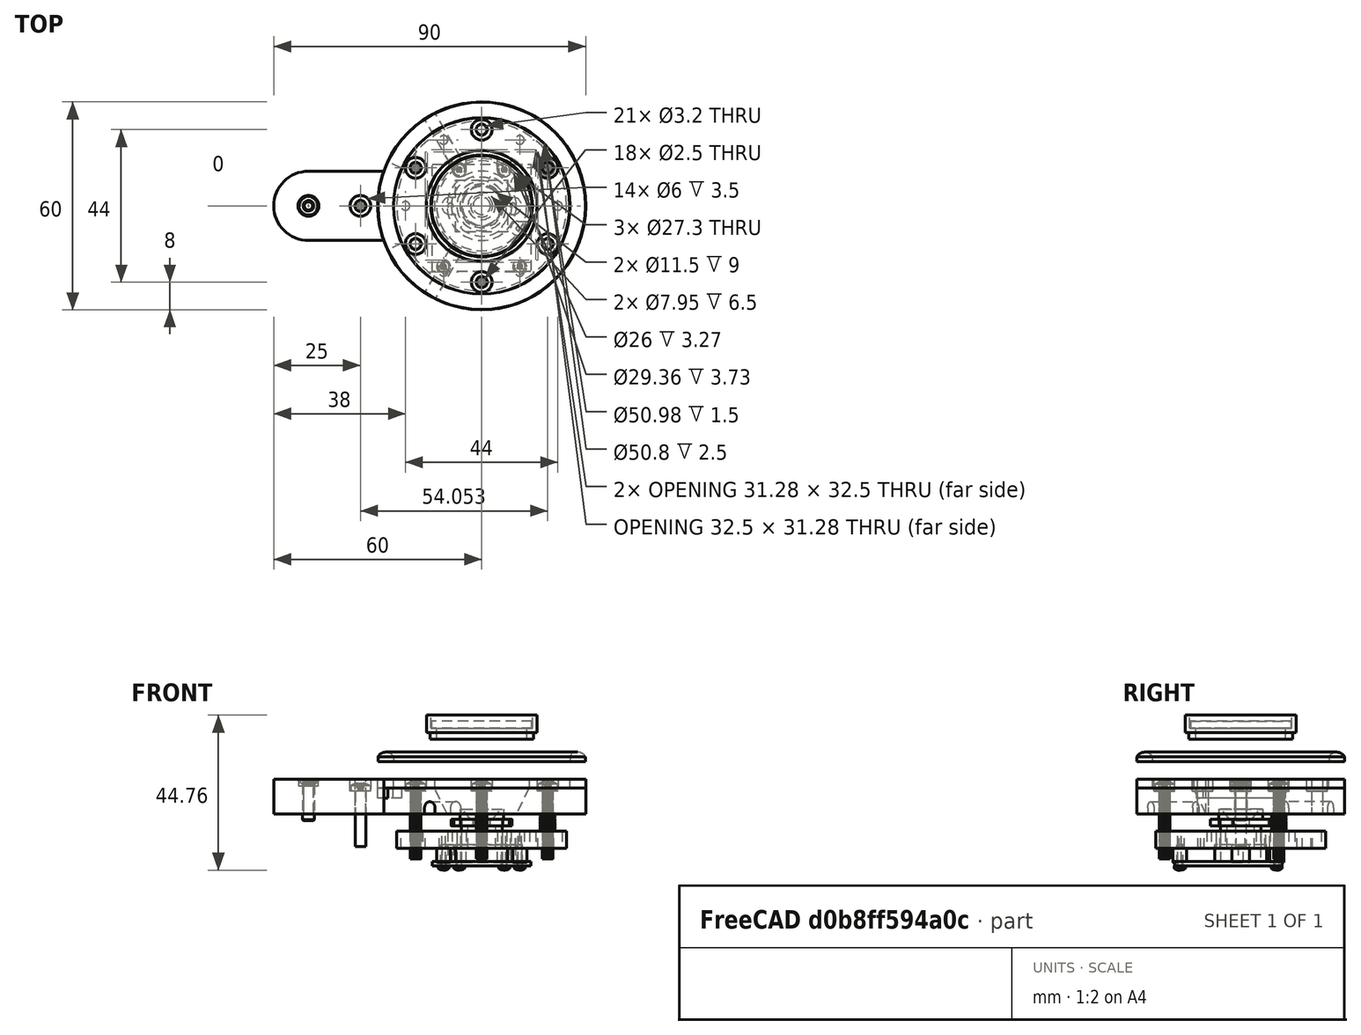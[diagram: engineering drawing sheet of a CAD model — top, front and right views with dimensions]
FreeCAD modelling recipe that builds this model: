
FCSTD DOCUMENT  (FreeCAD 0.15R4671 (Git))
Label: UpCam_base_v1
License: CreativeCommons Attribution-ShareAlike
LicenseURL: http://creativecommons.org/licenses/by-sa/4.0/
objects: Sketcher::SketchObject×10, Part::FeaturePython×10, Part::Feature×6, PartDesign::Pocket×5, PartDesign::Pad×4, Part::Mirroring×4, Part::Cut×2, PartDesign::Revolution×1, Part::MultiFuse×1
note: 53 computed .brp shape members not serialized (recipe doc carries the construction recipe); baked Part::Feature solids carry a one-line shape summary decoded from their .brp

FEATURE [Part::Feature] Compound  label="Philips SPZ5000 webcam"
  Placement = pos=(0,0,-15) rot=(0,0,1;1.5708rad)
  shape: bbox 28.5 x 31 x 16.4 mm, 52 faces, 3 solids (baked)
FEATURE [Sketcher::SketchObject] Sketch  label="camera base"
  sketch-geometry (20):
    g0: LineSegment [constr] StartX=-50 StartY=0 StartZ=0 EndX=0 EndY=0 EndZ=0
    g1: Circle CenterX=-50 CenterY=0 CenterZ=0 NormalX=0 NormalY=0 NormalZ=1 Radius=1.5
    g2: LineSegment StartX=-28.2843 StartY=10 StartZ=0 EndX=-50 EndY=10 EndZ=0
    g3: LineSegment StartX=-50 StartY=-10 StartZ=0 EndX=-28.2843 EndY=-10 EndZ=0
    g4: ArcOfCircle CenterX=-50 CenterY=0 CenterZ=0 NormalX=0 NormalY=0 NormalZ=1 Radius=10 StartAngle=1.5708 EndAngle=4.71239
    g5: ArcOfCircle CenterX=0 CenterY=0 CenterZ=0 NormalX=0 NormalY=0 NormalZ=1 Radius=30 StartAngle=3.48143 EndAngle=9.08494
    g6: Circle CenterX=-35 CenterY=0 CenterZ=0 NormalX=0 NormalY=0 NormalZ=1 Radius=1.6
    g7: LineSegment [constr] StartX=19.0526 StartY=-11 StartZ=0 EndX=19.0526 EndY=11 EndZ=0
    g8: LineSegment [constr] StartX=19.0526 StartY=11 StartZ=0 EndX=0 EndY=22 EndZ=0
    g9: LineSegment [constr] StartX=0 StartY=22 StartZ=0 EndX=-19.0526 EndY=11 EndZ=0
    g10: LineSegment [constr] StartX=-19.0526 StartY=11 StartZ=0 EndX=-19.0526 EndY=-11 EndZ=0
    g11: LineSegment [constr] StartX=-19.0526 StartY=-11 StartZ=0 EndX=0 EndY=-22 EndZ=0
    g12: LineSegment [constr] StartX=0 StartY=-22 StartZ=0 EndX=19.0526 EndY=-11 EndZ=0
    g13: Circle [constr] CenterX=0 CenterY=0 CenterZ=0 NormalX=0 NormalY=0 NormalZ=1 Radius=22
    g14: Circle CenterX=0 CenterY=22 CenterZ=0 NormalX=0 NormalY=0 NormalZ=1 Radius=1.6
    g15: Circle CenterX=-19.0526 CenterY=-11 CenterZ=0 NormalX=0 NormalY=0 NormalZ=1 Radius=1.6
    g16: Circle CenterX=19.0526 CenterY=-11 CenterZ=0 NormalX=0 NormalY=0 NormalZ=1 Radius=1.6
    g17: Circle CenterX=-19.0526 CenterY=11 CenterZ=0 NormalX=0 NormalY=0 NormalZ=1 Radius=1.6
    g18: Circle CenterX=0 CenterY=-22 CenterZ=0 NormalX=0 NormalY=0 NormalZ=1 Radius=1.6
    g19: Circle CenterX=19.0526 CenterY=11 CenterZ=0 NormalX=0 NormalY=0 NormalZ=1 Radius=1.6
  constraints (51):
    c: Horizontal(g0)
    c: DistanceX(g0) = 50
    c: Radius(g1) = 1.5
    c: Horizontal(g2)
    c: Horizontal(g3)
    c: Coincident(g4,g2)
    c: Coincident(g4,g3)
    c: Tangent(g4,g2)
    c: Radius(g4) = 10
    c: Coincident(g5,g0)
    c: Coincident(g5,g3)
    c: Coincident(g2,g5)
    c: Equal(g2,g3)
    c: DistanceX(g2,g3) = 0
    c: Coincident(g4,g1)
    c: Coincident(g0,g1)
    c: DistanceX(g0) = 0
    c: DistanceY(g0) = 0
    c: Radius(g5) = 30
    c: PointOnObject(g6,g0)
    c: DistanceX(g6,g0) = -15
    c: Coincident(g8,g9)
    c: Coincident(g9,g10)
    c: Coincident(g10,g11)
    c: Coincident(g11,g12)
    c: Coincident(g12,g7)
    c: Equal(g7, g8-g12) x5
    c: PointOnObject(g7,g13)
    c: PointOnObject(g8,g13)
    c: PointOnObject(g9,g13)
    c: PointOnObject(g10,g13)
    c: PointOnObject(g11,g13)
    c: PointOnObject(g12,g13)
    c: Coincident(g10,g-1)
    c: Coincident(g13,g-1)
    c: Radius(g13) = 22
    c: Coincident(g14,g8)
    c: Coincident(g15,g10)
    c: Coincident(g16,g7)
    c: Coincident(g17,g9)
    c: Coincident(g18,g11)
    c: Equal(g19,g16)
    c: Equal(g16,g18)
    c: Equal(g18,g15)
    c: Equal(g15,g17)
    c: Equal(g17,g14)
    c: Radius(g19) = 1.6
    c: Coincident(g19,g7)
    c: Coincident(g8,g7)
    c: Equal(g6,g14)
    c: Vertical(g10)
FEATURE [Sketcher::SketchObject] Sketch001
  Placement = pos=(0,0,0) rot=(1,0,0;1.5708rad)
  sketch-geometry (5):
    g0: LineSegment StartX=13.65 StartY=10 StartZ=0 EndX=13.65 EndY=7.5 EndZ=0
    g1: LineSegment StartX=13.65 StartY=7.5 StartZ=0 EndX=10 EndY=0 EndZ=0
    g2: LineSegment StartX=10 StartY=0 StartZ=0 EndX=0 EndY=0 EndZ=0
    g3: LineSegment StartX=0 StartY=0 StartZ=0 EndX=0 EndY=10 EndZ=0
    g4: LineSegment StartX=0 StartY=10 StartZ=0 EndX=13.65 EndY=10 EndZ=0
  constraints (14):
    c: Vertical(g0)
    c: Coincident(g0,g1)
    c: Coincident(g1,g2)
    c: Horizontal(g2)
    c: Coincident(g2,g3)
    c: Vertical(g3)
    c: Coincident(g3,g4)
    c: Coincident(g4,g0)
    c: Horizontal(g4)
    c: DistanceX(g2) = -10
    c: DistanceX(g4) = 13.65
    c: DistanceY(g0) = -2.5
    c: DistanceY(g3) = 10
    c: Coincident(g2,g-1)
FEATURE [PartDesign::Revolution] Revolution
  Angle = 360
  Axis = (0,0,1)
  Base = (0,0,0)
  Placement = pos=(0,0,0) rot=(1,0,0;1.5708rad)
  ReferenceAxis = -> Sketch001 [V_Axis]
  Reversed = true
  Sketch = -> Sketch001
FEATURE [PartDesign::Pad] Pad
  Length = 10
  Length2 = 100
  Sketch = -> Sketch
  Type = 0
FEATURE [Part::Cut] Cut
  Base = -> Pad
  Tool = -> Revolution
FEATURE [Sketcher::SketchObject] Sketch002
  ExternalGeometry = -> [Cut]
  Placement = pos=(0,0,10) rot=(0,0,1;0rad)
  Support = -> Cut [Face5]
  sketch-geometry (7):
    g0: Circle CenterX=-35 CenterY=0 CenterZ=0 NormalX=0 NormalY=0 NormalZ=1 Radius=3
    g1: Circle CenterX=-19.0526 CenterY=11 CenterZ=0 NormalX=0 NormalY=0 NormalZ=1 Radius=3
    g2: Circle CenterX=-19.0526 CenterY=-11 CenterZ=0 NormalX=0 NormalY=0 NormalZ=1 Radius=3
    g3: Circle CenterX=0 CenterY=22 CenterZ=0 NormalX=0 NormalY=0 NormalZ=1 Radius=3
    g4: Circle CenterX=19.0526 CenterY=-11 CenterZ=0 NormalX=0 NormalY=0 NormalZ=1 Radius=3
    g5: Circle CenterX=19.0526 CenterY=11 CenterZ=0 NormalX=0 NormalY=0 NormalZ=1 Radius=3
    g6: Circle CenterX=0 CenterY=-22 CenterZ=0 NormalX=0 NormalY=0 NormalZ=1 Radius=3
  constraints (14):
    c: Coincident(g0,g-7)
    c: Radius(g0) = 3
    c: Coincident(g1,g-6)
    c: Coincident(g2,g-5)
    c: Coincident(g3,g-4)
    c: Coincident(g4,g-9)
    c: Coincident(g5,g-8)
    c: Equal(g5,g0)
    c: Equal(g0,g1)
    c: Equal(g1,g2)
    c: Equal(g2,g3)
    c: Equal(g3,g4)
    c: Coincident(g6,g-10)
    c: Equal(g6,g5)
FEATURE [PartDesign::Pocket] Pocket
  Length = 3.5
  Sketch = -> Sketch002
  Type = 0
FEATURE [Sketcher::SketchObject] Sketch004
  ExternalGeometry = -> [Pocket]
  Placement = pos=(0,0,10) rot=(0,0,1;0rad)
  Support = -> Pocket [Face5]
  sketch-geometry (2):
    g0: Circle CenterX=0 CenterY=0 CenterZ=0 NormalX=0 NormalY=0 NormalZ=1 Radius=25.4
    g1: Circle CenterX=0 CenterY=0 CenterZ=0 NormalX=0 NormalY=0 NormalZ=1 Radius=30
  constraints (4):
    c: Coincident(g0,g-1)
    c: Radius(g0) = 25.4
    c: Coincident(g1,g-1)
    c: PointOnObject(g-3,g1)
FEATURE [PartDesign::Pocket] Pocket001
  Length = 2.5
  Sketch = -> Sketch004
  Type = 0
FEATURE [Sketcher::SketchObject] Sketch003
  ExternalGeometry = -> [Pocket,Pocket001]
  Placement = pos=(0,0,7.5) rot=(0,0,1;0rad)
  Support = -> Pocket001 [Face7]
  sketch-geometry (6):
    g0: ArcOfCircle CenterX=0 CenterY=0 CenterZ=0 NormalX=0 NormalY=0 NormalZ=1 Radius=25.56 StartAngle=2.70171 EndAngle=3.58147
    g1: LineSegment [constr] StartX=0 StartY=0 StartZ=0 EndX=-23.1268 EndY=10.8842 EndZ=0
    g2: LineSegment StartX=-23.1268 StartY=10.8842 StartZ=0 EndX=-27.1441 EndY=12.7749 EndZ=0
    g3: LineSegment [constr] StartX=0 StartY=0 StartZ=0 EndX=-23.1268 EndY=-10.8842 EndZ=0
    g4: LineSegment StartX=-23.1268 StartY=-10.8842 StartZ=0 EndX=-27.1441 EndY=-12.7749 EndZ=0
    g5: ArcOfCircle CenterX=0 CenterY=0 CenterZ=0 NormalX=0 NormalY=0 NormalZ=1 Radius=30 StartAngle=2.70171 EndAngle=3.58147
  constraints (18):
    c: PointOnObject(g4,g-4)
    c: Equal(g1,g3)
    c: Equal(g2,g4)
    c: Coincident(g0,g3)
    c: Coincident(g0,g4)
    c: Coincident(g0,g1)
    c: Coincident(g0,g2)
    c: Distance(g2) = 4.44
    c: Coincident(g2,g5)
    c: DistanceX(g0,g0) = 0
    c: Distance(g4,g-4) = 3
    c: Parallel(g4,g3)
    c: Parallel(g1,g2)
    c: Coincident(g4,g5)
    c: Coincident(g1,g-1)
    c: Coincident(g3,g-1)
    c: Coincident(g0,g-1)
    c: Coincident(g5,g-1)
FEATURE [PartDesign::Pocket] Pocket002
  Length = 3
  Sketch = -> Sketch003
  Type = 0
FEATURE [Sketcher::SketchObject] Sketch005
  ExternalGeometry = -> [Pocket002]
  Placement = pos=(0,0,10) rot=(0,0,1;0rad)
  Support = -> Pocket002 [Face5]
  sketch-geometry (1):
    g0: Circle CenterX=-35 CenterY=0 CenterZ=0 NormalX=0 NormalY=0 NormalZ=1 Radius=2.8
  constraints (2):
    c: Coincident(g0,g-3)
    c: Radius(g0) = 2.8
FEATURE [PartDesign::Pocket] Pocket003  label="camera base"
  Length = 2
  Sketch = -> Sketch005
  Type = 0
FEATURE [Sketcher::SketchObject] Sketch006
  Placement = pos=(0,0,-5) rot=(1,0,0;3.14159rad)
  sketch-geometry (35):
    g0: LineSegment [constr] StartX=22 StartY=0 StartZ=0 EndX=11 EndY=19.0526 EndZ=0
    g1: LineSegment [constr] StartX=11 StartY=19.0526 StartZ=0 EndX=-11 EndY=19.0526 EndZ=0
    g2: LineSegment [constr] StartX=-11 StartY=19.0526 StartZ=0 EndX=-22 EndY=0 EndZ=0
    g3: LineSegment [constr] StartX=-22 StartY=0 StartZ=0 EndX=-11 EndY=-19.0526 EndZ=0
    g4: LineSegment [constr] StartX=-11 StartY=-19.0526 StartZ=0 EndX=11 EndY=-19.0526 EndZ=0
    g5: LineSegment [constr] StartX=11 StartY=-19.0526 StartZ=0 EndX=22 EndY=0 EndZ=0
    g6: Circle [constr] CenterX=0 CenterY=0 CenterZ=0 NormalX=0 NormalY=0 NormalZ=1 Radius=22
    g7: ArcOfCircle CenterX=10.4 CenterY=-6.5 CenterZ=0 NormalX=0 NormalY=0 NormalZ=1 Radius=2 StartAngle=1.5708 EndAngle=4.71239
    g8: LineSegment StartX=10.4 StartY=-8.5 StartZ=0 EndX=13.8496 EndY=-8.5 EndZ=0
    g9: LineSegment StartX=10.4 StartY=-4.5 StartZ=0 EndX=15.6145 EndY=-4.5 EndZ=0
    g10: ArcOfCircle CenterX=10.4 CenterY=6.5 CenterZ=0 NormalX=0 NormalY=0 NormalZ=1 Radius=2 StartAngle=1.5708 EndAngle=4.71239
    g11: LineSegment StartX=10.4 StartY=4.5 StartZ=0 EndX=15.6145 EndY=4.5 EndZ=0
    g12: LineSegment StartX=10.4 StartY=8.5 StartZ=0 EndX=13.8496 EndY=8.5 EndZ=0
    g13: Circle CenterX=0 CenterY=0 CenterZ=0 NormalX=0 NormalY=0 NormalZ=1 Radius=24.5
    g14: ArcOfCircle CenterX=0 CenterY=0 CenterZ=0 NormalX=0 NormalY=0 NormalZ=1 Radius=16.25 StartAngle=0.550457 EndAngle=5.73273
    g15: LineSegment [constr] StartX=10.4 StartY=6.5 StartZ=0 EndX=10.4 EndY=-6.5 EndZ=0
    g16: LineSegment [constr] StartX=10.4 StartY=-6.5 StartZ=0 EndX=-17.6 EndY=-11 EndZ=0
    g17: LineSegment [constr] StartX=-17.6 StartY=-11 StartZ=0 EndX=-17.6 EndY=11 EndZ=0
    g18: LineSegment [constr] StartX=-17.6 StartY=11 StartZ=0 EndX=10.4 EndY=6.5 EndZ=0
    g19: LineSegment [constr] StartX=10.4 StartY=6.5 StartZ=0 EndX=-17.6 EndY=-11 EndZ=0
    g20: LineSegment [constr] StartX=-17.6 StartY=11 StartZ=0 EndX=10.4 EndY=-6.5 EndZ=0
    g21: GeomPoint [constr] X=0 Y=0 Z=0
    g22: ArcOfCircle CenterX=0 CenterY=0 CenterZ=0 NormalX=0 NormalY=0 NormalZ=1 Radius=16.25 StartAngle=6.00259 EndAngle=6.56378
    g23: Circle CenterX=11 CenterY=19.0526 CenterZ=0 NormalX=0 NormalY=0 NormalZ=1 Radius=1.25
    g24: Circle CenterX=-11 CenterY=19.0526 CenterZ=0 NormalX=0 NormalY=0 NormalZ=1 Radius=1.25
    g25: Circle CenterX=-22 CenterY=0 CenterZ=0 NormalX=0 NormalY=0 NormalZ=1 Radius=1.25
    g26: Circle CenterX=22 CenterY=0 CenterZ=0 NormalX=0 NormalY=0 NormalZ=1 Radius=1.25
    g27: Circle CenterX=11 CenterY=-19.0526 CenterZ=0 NormalX=0 NormalY=0 NormalZ=1 Radius=1.25
    g28: Circle CenterX=-11 CenterY=-19.0526 CenterZ=0 NormalX=0 NormalY=0 NormalZ=1 Radius=1.25
    g29: Circle CenterX=10.4 CenterY=6.5 CenterZ=0 NormalX=0 NormalY=0 NormalZ=1 Radius=0.5
    g30: Circle CenterX=10.4 CenterY=-6.5 CenterZ=0 NormalX=0 NormalY=0 NormalZ=1 Radius=0.5
    g31: Circle CenterX=-17.6 CenterY=11 CenterZ=0 NormalX=0 NormalY=0 NormalZ=1 Radius=0.5
    g32: Circle CenterX=-17.6 CenterY=-11 CenterZ=0 NormalX=0 NormalY=0 NormalZ=1 Radius=0.5
    g33: LineSegment [constr] StartX=-17.6 StartY=11 StartZ=0 EndX=-13.78 EndY=8.61248 EndZ=0
    g34: LineSegment [constr] StartX=-16.25 StartY=0 StartZ=0 EndX=-20.75 EndY=0 EndZ=0
  constraints (83):
    c: Coincident(g0,g1)
    c: Coincident(g1,g2)
    c: Coincident(g2,g3)
    c: Coincident(g3,g4)
    c: Coincident(g4,g5)
    c: Coincident(g5,g0)
    c: Equal(g0, g1-g5) x5
    c: PointOnObject(g0,g6)
    c: PointOnObject(g1,g6)
    c: PointOnObject(g2,g6)
    c: PointOnObject(g3,g6)
    c: PointOnObject(g4,g6)
    c: PointOnObject(g5,g6)
    c: Coincident(g3,g-1)
    c: Coincident(g6,g-1)
    c: Tangent(g7,g9) = 1.5708
    c: Tangent(g7,g8) = -1.5708
    c: Horizontal(g8)
    c: Tangent(g10,g12) = 1.5708
    c: Tangent(g10,g11) = -1.5708
    c: Horizontal(g11)
    c: Coincident(g13,g-1)
    c: Radius(g13) = 24.5
    c: Horizontal(g12)
    c: Horizontal(g9)
    c: Equal(g7,g10)
    c: Coincident(g14,g-1)
    c: Coincident(g15,g10)
    c: Coincident(g15,g7)
    c: Vertical(g15)
    c: Coincident(g15,g16)
    c: Coincident(g16,g17)
    c: Vertical(g17)
    c: Coincident(g17,g18)
    c: Coincident(g18,g15)
    c: Equal(g18,g16)
    c: DistanceY(g15) = -13
    c: DistanceY(g17) = 22
    c: Coincident(g19,g10)
    c: Coincident(g19,g16)
    c: Coincident(g20,g17)
    c: Coincident(g20,g7)
    c: PointOnObject(g21,g20)
    c: PointOnObject(g21,g19)
    c: Coincident(g21,g-1)
    c: DistanceX(g16,g7) = 28
    c: Radius(g10) = 2
    c: Coincident(g14,g12)
    c: Coincident(g22,g11)
    c: Equal(g14,g22)
    c: Coincident(g14,g8)
    c: Coincident(g22,g9)
    c: Coincident(g14,g22)
    c: Radius(g6) = 22
    c: Horizontal(g1)
    c: Coincident(g23,g0)
    c: Coincident(g24,g1)
    c: Coincident(g25,g2)
    c: Coincident(g26,g0)
    c: Coincident(g27,g4)
    c: Coincident(g28,g3)
    c: Equal(g28,g27)
    c: Equal(g27,g26)
    c: Equal(g26,g23)
    c: Equal(g23,g24)
    c: Equal(g24,g25)
    c: Radius(g23) = 1.25
    c: Coincident(g29,g10)
    c: Coincident(g30,g7)
    c: Coincident(g31,g17)
    c: Coincident(g32,g16)
    c: Equal(g32,g31)
    c: Equal(g31,g30)
    c: Equal(g30,g29)
    c: Radius(g31) = 0.5
    c: Coincident(g33,g17)
    c: PointOnObject(g33,g14)
    c: Perpendicular(g14,g33)
    c: PointOnObject(g34,g14)
    c: PointOnObject(g34,g25)
    c: Horizontal(g34)
    c: Perpendicular(g14,g34)
    c: DistanceX(g34) = -4.5
FEATURE [PartDesign::Pad] Pad001
  Length = 5
  Length2 = 100
  Placement = pos=(0,0,-5) rot=(1,0,0;3.14159rad)
  Sketch = -> Sketch006
  Type = 0
FEATURE [Sketcher::SketchObject] Sketch007
  ExternalGeometry = -> [Pad001]
  Placement = pos=(0,0,-10) rot=(1,0,0;3.14159rad)
  Support = -> Pad001 [Face21]
  sketch-geometry (8):
    g0: Circle CenterX=-17.6 CenterY=11 CenterZ=0 NormalX=0 NormalY=0 NormalZ=1 Radius=2
    g1: Circle CenterX=-17.6 CenterY=-11 CenterZ=0 NormalX=0 NormalY=0 NormalZ=1 Radius=2
    g2: Circle CenterX=10.4 CenterY=-6.5 CenterZ=0 NormalX=0 NormalY=0 NormalZ=1 Radius=2
    g3: Circle CenterX=10.4 CenterY=6.5 CenterZ=0 NormalX=0 NormalY=0 NormalZ=1 Radius=2
    g4: Circle CenterX=-17.6 CenterY=11 CenterZ=0 NormalX=0 NormalY=0 NormalZ=1 Radius=0.5
    g5: Circle CenterX=-17.6 CenterY=-11 CenterZ=0 NormalX=0 NormalY=0 NormalZ=1 Radius=0.5
    g6: Circle CenterX=10.4 CenterY=6.5 CenterZ=0 NormalX=0 NormalY=0 NormalZ=1 Radius=0.5
    g7: Circle CenterX=10.4 CenterY=-6.5 CenterZ=0 NormalX=0 NormalY=0 NormalZ=1 Radius=0.5
  constraints (16):
    c: Coincident(g0,g-3)
    c: Coincident(g1,g-4)
    c: Coincident(g2,g-8)
    c: Equal(g2,g-8)
    c: Coincident(g3,g-7)
    c: Equal(g3,g2)
    c: Equal(g1,g0)
    c: Coincident(g0,g4)
    c: Coincident(g5,g1)
    c: Coincident(g6,g3)
    c: Coincident(g7,g2)
    c: Equal(g7,g6)
    c: Equal(g6,g4)
    c: Equal(g4,g5)
    c: Equal(g4,g-3)
    c: Equal(g0,g3)
FEATURE [PartDesign::Pad] Pad002
  Length = 4
  Length2 = 100
  Placement = pos=(0,0,-5) rot=(1,0,0;3.14159rad)
  Sketch = -> Sketch007
  Type = 0
FEATURE [Part::FeaturePython] Screw  label="M1.6x6-Screw"  # Fasteners workbench fastener (typed FeaturePython)
  Placement = pos=(11,-17.5,-15) rot=(1,0,0;3.14159rad)
  baseObject = -> Compound [Edge20]
  diameter = 1
  invert = true
  length = 3
  matchOuter = false
  offset = 0
  thread = false
  type = 16
FEATURE [Part::Mirroring] Part__Mirroring  label="Pad002 (print)"
  Base = (0,0,0)
  Normal = (0,0,1)
  Source = -> Pad002
FEATURE [Part::Mirroring] Part__Mirroring001  label="Pad002 (print) (Mirror #2)"
  Base = (0,0,0)
  Normal = (0,0,1)
  Placement = pos=(0,0,0) rot=(0,0,1;1.5708rad)
  Source = -> Part__Mirroring
FEATURE [Sketcher::SketchObject] Sketch008  label="cable way"
  Placement = pos=(-7.5,-12.9904,0) rot=(0.935113,-0.250563,-0.250563;1.63783rad)
  sketch-geometry (4):
    g0: ArcOfCircle CenterX=0 CenterY=1.75 CenterZ=0 NormalX=0 NormalY=0 NormalZ=1 Radius=1.75 StartAngle=0 EndAngle=3.14159
    g1: LineSegment StartX=-1.75 StartY=1.75 StartZ=0 EndX=-1.75 EndY=0 EndZ=0
    g2: LineSegment StartX=1.75 StartY=1.75 StartZ=0 EndX=1.75 EndY=0 EndZ=0
    g3: LineSegment StartX=-1.75 StartY=0 StartZ=0 EndX=1.75 EndY=0 EndZ=0
  constraints (11):
    c: Tangent(g0,g2) = 1.5708
    c: Tangent(g0,g1) = -1.5708
    c: Vertical(g1)
    c: PointOnObject(g0,g-2)
    c: Radius(g0) = 1.75
    c: PointOnObject(g2,g-1)
    c: Equal(g1,g2)
    c: Vertical(g2)
    c: DistanceY(g1) = -1.75
    c: Coincident(g3,g1)
    c: Coincident(g3,g2)
FEATURE [PartDesign::Pad] Pad003  label="cable way cut"
  Length = 20
  Length2 = 100
  Placement = pos=(-7.5,-12.9904,0) rot=(0.935113,-0.250563,-0.250563;1.63783rad)
  Sketch = -> Sketch008
  Type = 0
FEATURE [Part::Mirroring] Part__Mirroring002  label="cable way cut (Mirror #3)"
  Base = (0,0,0)
  Normal = (0,1,0)
  Source = -> Pad003
FEATURE [Part::MultiFuse] Fusion
  Shapes = -> [Part__Mirroring002,Pad003]
FEATURE [Part::Cut] Cut001  label="camera base"
  Base = -> Pocket003
  Tool = -> Fusion
FEATURE [Sketcher::SketchObject] Sketch009
  ExternalGeometry = -> [Cut001]
  Placement = pos=(0,0,10) rot=(0,0,1;0rad)
  Support = -> Cut001 [Face6]
  sketch-geometry (1):
    g0: Circle CenterX=-50 CenterY=0 CenterZ=0 NormalX=0 NormalY=0 NormalZ=1 Radius=2.75
  constraints (2):
    c: Coincident(g0,g-3)
    c: Radius(g0) = 2.75
FEATURE [PartDesign::Pocket] Pocket004
  Length = 2
  Sketch = -> Sketch009
  Type = 0
FEATURE [Part::FeaturePython] Screw001  label="M1.6x6-Screw"  # Fasteners workbench fastener (typed FeaturePython)
  Placement = pos=(-11,-17.6,-15) rot=(1,0,0;3.14159rad)
  baseObject = -> Part__Mirroring001 [Edge58]
  diameter = 1
  invert = false
  length = 3
  matchOuter = false
  offset = 1
  thread = false
  type = 16
FEATURE [Part::FeaturePython] Screw002  label="M1.6x6-Screw"  # Fasteners workbench fastener (typed FeaturePython)
  Placement = pos=(-6.5,10.4,-15) rot=(1,0,0;3.14159rad)
  baseObject = -> Part__Mirroring001 [Edge65]
  diameter = 1
  invert = false
  length = 3
  matchOuter = false
  offset = 1
  thread = false
  type = 16
FEATURE [Part::FeaturePython] Screw003  label="M1.6x6-Screw"  # Fasteners workbench fastener (typed FeaturePython)
  Placement = pos=(6.5,10.4,-15) rot=(1,0,0;3.14159rad)
  baseObject = -> Part__Mirroring001 [Edge62]
  diameter = 1
  invert = false
  length = 3
  matchOuter = false
  offset = 1
  thread = false
  type = 16
FEATURE [Part::FeaturePython] Screw004  label="M3x20-Screw"  # Fasteners workbench fastener (typed FeaturePython)
  Placement = pos=(19.0526,11,7) rot=(0,0,1;0rad)
  baseObject = -> Part__Mirroring001 [Edge17]
  diameter = 4
  invert = true
  length = 8
  matchOuter = false
  offset = 12
  thread = true
  type = 16
FEATURE [Part::FeaturePython] Screw005  label="M3x20-Screw"  # Fasteners workbench fastener (typed FeaturePython)
  Placement = pos=(-19.0526,11,7) rot=(0,0,1;0rad)
  baseObject = -> Part__Mirroring001 [Edge15]
  diameter = 4
  invert = true
  length = 8
  matchOuter = false
  offset = 12
  thread = true
  type = 16
FEATURE [Part::FeaturePython] Screw006  label="M3x20-Screw"  # Fasteners workbench fastener (typed FeaturePython)
  Placement = pos=(0,-22,7) rot=(0,0,1;0rad)
  baseObject = -> Part__Mirroring001 [Edge13]
  diameter = 4
  invert = true
  length = 8
  matchOuter = false
  offset = 12
  thread = true
  type = 16
FEATURE [Part::FeaturePython] Screw007  label="M3x12-Screw"  # Fasteners workbench fastener (typed FeaturePython)
  Placement = pos=(-50,0,10) rot=(0,0,1;0rad)
  baseObject = -> Pocket004 [Edge79]
  diameter = 1
  invert = true
  length = 2
  matchOuter = true
  offset = 2
  thread = false
  type = 3
FEATURE [Part::FeaturePython] Stud  label="M3.5x12-Stud"  # WARN: FeaturePython — macro-defined, semantics opaque (R4)
  Placement = pos=(-50,0,10) rot=(0,0,1;0rad)
  baseObject = -> Pocket004 [Edge79]
  diameter = 3
  invert = true
  length = 3
  offset = 2
FEATURE [Part::FeaturePython] Screw008  label="M3x16-Screw"  # Fasteners workbench fastener (typed FeaturePython)
  Placement = pos=(-35,0,6.5) rot=(0,0,1;0rad)
  baseObject = -> Pocket004 [Edge81]
  diameter = 4
  invert = true
  length = 7
  matchOuter = true
  offset = 0
  thread = false
  type = 16
FEATURE [Part::Feature] Compound002  label="UpCamComplex"
  shape: bbox 90 x 60 x 26.26 mm, 354 faces, 14 solids (baked)
FEATURE [Part::Feature] Compound004  label="spring 4x10x0.3mm"
  Placement = pos=(-19,11,-5) rot=(0,0,1;0rad)
  shape: bbox 6.091 x 6.812 x 5.575 mm, 16 faces, 3 solids (baked)
FEATURE [Part::Mirroring] Part__Mirroring003  label="spring 4x10x0.3mm (Mirror #4)"
  Base = (0,0,0)
  Normal = (1,0,0)
  Source = -> Compound004
FEATURE [Part::Feature] Revolution001  label="Angels eyes LED ring"
  Placement = pos=(0,0,15) rot=(1,0,0;1.5708rad)
  shape: bbox 65.48 x 65.48 x 2.8 mm, 4 faces (baked)
FEATURE [Part::Feature] Revolution002  label="UV filter ring"
  Placement = pos=(0,0,21.5) rot=(0,0,1;0rad)
  shape: bbox 31.9 x 31.9 x 7 mm, 8 faces (baked)
FEATURE [Part::Feature] Pad004  label="UV glass"
  Placement = pos=(0,0,21.4) rot=(0,0,1;0rad)
  shape: bbox 29 x 29 x 2 mm, 3 faces (baked)
